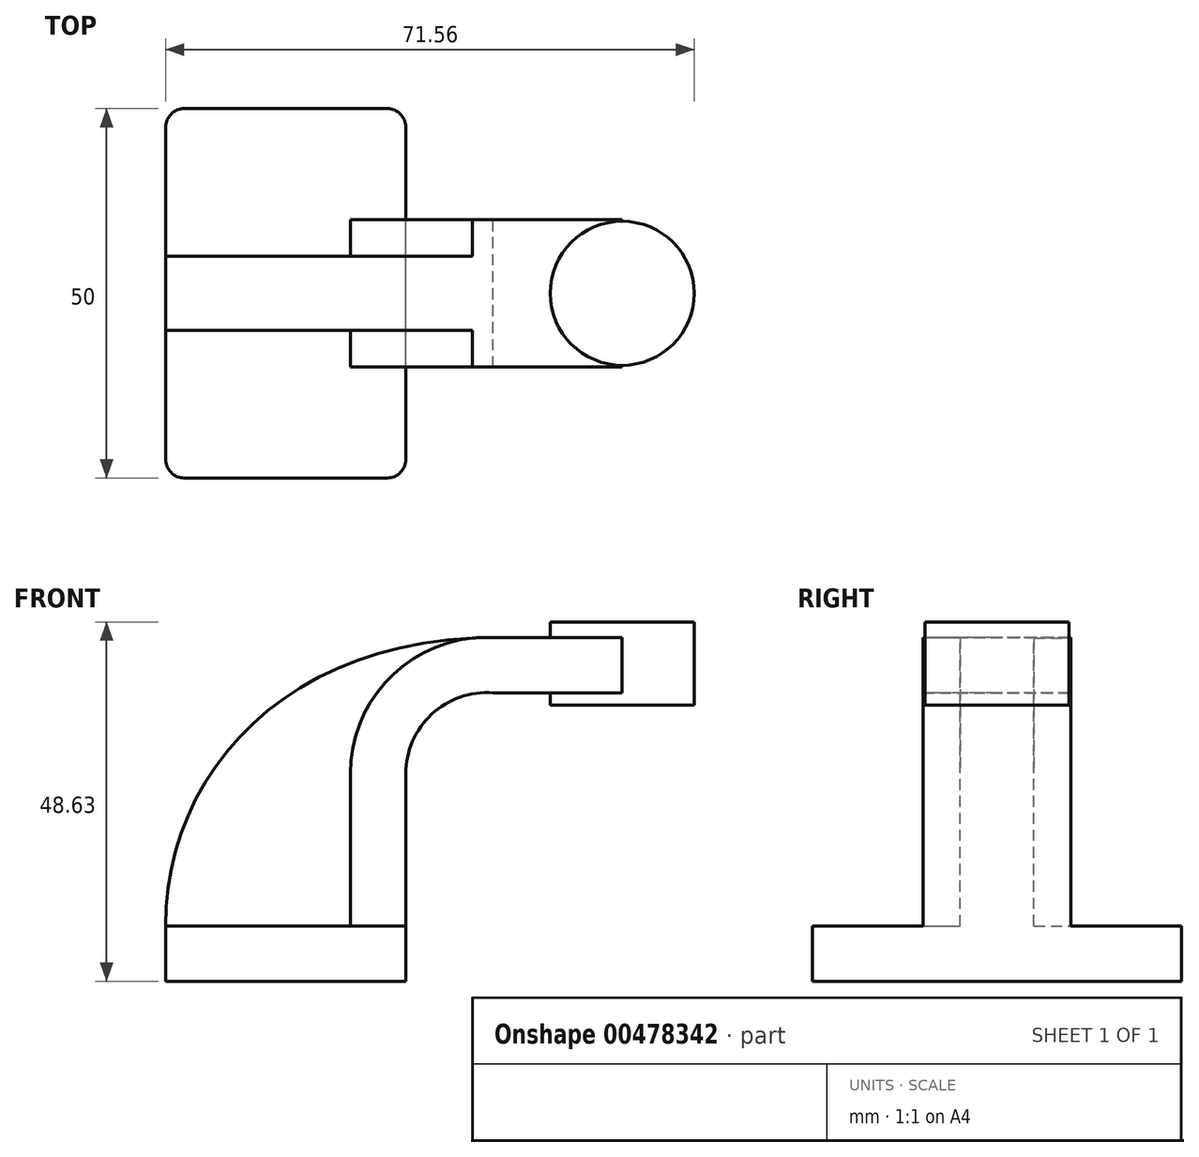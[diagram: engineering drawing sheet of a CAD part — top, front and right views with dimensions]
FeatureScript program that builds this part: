
annotation { "Feature Type Name" : "Feature", "Feature Type Description" : "" }
export const myFeature = defineFeature(function(context is Context, id is Id, definition is map)
    precondition{}
    {
        {
            var Q0;
            Q0=qCreatedBy(makeId("Front.planeOp"),FACE);
            var sketch = newSketch(context, id + "F0", { "sketchPlane" : qUnion([Q0])});
            skLineSegment(sketch, "E0.bottom", {"start": v(-1.63, -0.38) * mm, "end": v(1.63, -0.38) * mm});
            skLineSegment(sketch, "E0.top", {"start": v(-1.63, 0.37) * mm, "end": v(1.63, 0.37) * mm});
            skLineSegment(sketch, "E0.left", {"start": v(-1.63, -0.38) * mm, "end": v(-1.63, 0.37) * mm});
            skLineSegment(sketch, "E0.right", {"start": v(1.62, -0.38) * mm, "end": v(1.63, 0.37) * mm});
            skPoint(sketch, "E0.middle", {"position": v(0, 0) * mm});
            skLineSegment(sketch, "E1", {"start": v(1.63, 0.37) * mm, "end": v(1.63, 2.43) * mm});
            skArc(sketch, "E2", {"start": v(1.63, 2.43) * mm, "mid": v(1.98, 3.24) * mm, "end": v(2.8, 3.53) * mm});
            skLineSegment(sketch, "E3", {"start": v(2.8, 3.53) * mm, "end": v(4.56, 3.53) * mm});
            skLineSegment(sketch, "E4.bottom", {"start": v(3.53, 3.36) * mm, "end": v(5.53, 3.36) * mm});
            skLineSegment(sketch, "E4.top", {"start": v(3.53, 4.49) * mm, "end": v(5.53, 4.49) * mm});
            skLineSegment(sketch, "E4.left", {"start": v(3.53, 3.36) * mm, "end": v(3.53, 4.49) * mm});
            skLineSegment(sketch, "E4.right", {"start": v(5.53, 3.36) * mm, "end": v(5.53, 4.49) * mm});
            skPoint(sketch, "E4.middle", {"position": v(4.53, 3.93) * mm});
            skLineSegment(sketch, "E5.0", {"start": v(2.83, 4.28) * mm, "end": v(4.56, 4.28) * mm});
            skArc(sketch, "E5.1", {"start": v(0.88, 2.43) * mm, "mid": v(1.45, 3.78) * mm, "end": v(2.83, 4.28) * mm});
            skLineSegment(sketch, "E5.2", {"start": v(0.88, 0.37) * mm, "end": v(0.88, 2.43) * mm});
            skLineSegment(sketch, "E6", {"start": v(4.56, 3.36) * mm, "end": v(4.56, 4.49) * mm});
            skFitSpline(sketch, "E7", {"points": [v(-1.63, 0.37) * mm, v(2.83, 4.28) * mm], "startDerivative": vector(0, 6.18) * mm, "endDerivative": vector(8.5, 0) * mm});
            skSolve(sketch);
        }
        {
            var Q0;
            Q0=makeQuery(id+"F0.imprint","IMPRINT",FACE,{"disambiguationData":[TD([[makeQuery(id+"F0.imprint","IMPRINT",EDGE,{"derivedFrom":sQuery(id+"F0.wireOp",EDGE,"E0.bottom")}),1.0]])]});
            extrude(context, id + "F1", {"entities" : qUnion([Q0]), "endBound" : BoundingType.SYMMETRIC, "depth" : 5 * mm});
        }
        {
            var Q0;
            {var subQ7=sQuery(id+"F0.wireOp",EDGE,"E1");Q0=makeQuery(id+"F0.imprint","IMPRINT",FACE,{"disambiguationData":[TD([[makeQuery(id+"F0.imprint","IMPRINT",EDGE,{"derivedFrom":subQ7}),1.0]])]});}
            var Q1;
            {var subQ0=sQuery(id+"F0.wireOp",EDGE,"E6");var subQ1=sQuery(id+"F0.wireOp",EDGE,"E3");var subQ2=makeQuery(id+"F0.imprint","INTERSECT",VERTEX,{"derivedFrom":[subQ1,subQ0]});Q1=makeQuery(id+"F0.imprint","IMPRINT",FACE,{"disambiguationData":[TD([[makeQuery(id+"F0.imprint","IMPRINT",EDGE,{"disambiguationData":[TD([[subQ2,1.0]])],"derivedFrom":subQ1}),1.0]])]});}
            extrude(context, id + "F2", {"entities" : qUnion([Q0, Q1]), "operationType" : NewBodyOperationType.ADD, "endBound" : BoundingType.SYMMETRIC, "depth" : 2 * mm});
        }
        {
            var Q0;
            {var subQ3=sQuery(id+"F0.wireOp",EDGE,"E5.2");Q0=makeQuery(id+"F0.imprint","IMPRINT",FACE,{"disambiguationData":[TD([[makeQuery(id+"F0.imprint","IMPRINT",EDGE,{"derivedFrom":subQ3}),1.0]])]});}
            extrude(context, id + "F3", {"entities" : qUnion([Q0]), "operationType" : NewBodyOperationType.ADD, "endBound" : BoundingType.SYMMETRIC, "depth" : 1 * mm});
        }
        {
            var Q0;
            {var subQ0=sQuery(id+"F0.wireOp",EDGE,"E4.right");Q0=makeQuery(id+"F0.imprint","IMPRINT",FACE,{"disambiguationData":[TD([[makeQuery(id+"F0.imprint","IMPRINT",EDGE,{"derivedFrom":subQ0}),1.0]])]});}
            var Q1;
            Q1=sQuery(id+"F0.wireOp",EDGE,"E6");
            revolve(context, id + "F4", {"operationType" : NewBodyOperationType.ADD, "entities" : qUnion([Q0]), "axis" : qUnion([Q1]), "revolveType" : RevolveType.FULL});
        }
        {
            var Q0;
            Q0=makeQuery(id+"F1.opExtrude","CAP_EDGE",EDGE,{"disambiguationData":[OSD([sQuery(id+"F0.wireOp",EDGE,"E0.right")])],"isStart":false});
            var Q1;
            Q1=makeQuery(id+"F1.opExtrude","CAP_EDGE",EDGE,{"disambiguationData":[OSD([sQuery(id+"F0.wireOp",EDGE,"E0.left")])],"isStart":false});
            var Q2;
            Q2=makeQuery(id+"F1.opExtrude","CAP_EDGE",EDGE,{"disambiguationData":[OSD([sQuery(id+"F0.wireOp",EDGE,"E0.right")])],"isStart":true});
            var Q3;
            Q3=makeQuery(id+"F1.opExtrude","CAP_EDGE",EDGE,{"disambiguationData":[OSD([sQuery(id+"F0.wireOp",EDGE,"E0.left")])],"isStart":true});
            fillet(context, id + "F5", {"entities" : qUnion([Q0, Q1, Q2, Q3]), "radius" : 0.25 * mm, "tangentPropagation" : true, "allowEdgeOverflow" : false});
        }
        {
            var Q0;
            Q0=makeQuery(id+"F1.opExtrude","SWEPT_BODY",BODY,{"disambiguationData":[OSD([sQuery(id+"F0.wireOp",EDGE,"E0.bottom"),sQuery(id+"F0.wireOp",EDGE,"E0.top"),sQuery(id+"F0.wireOp",EDGE,"E0.left"),sQuery(id+"F0.wireOp",EDGE,"E0.right")])]});
            var Q1;
            Q1=qCreatedBy(makeId("Origin.pointOp"),VERTEX);
            transform(context, id + "F6", {"entities" : qUnion([Q0]), "transformType" : TransformType.SCALE_UNIFORMLY, "scale" : 10, "scalePoint" : qUnion([Q1]), "makeCopy" : false});
        }
    });
